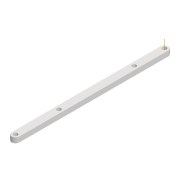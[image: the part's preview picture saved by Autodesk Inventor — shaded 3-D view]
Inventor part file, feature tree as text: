
AUTODESK INVENTOR PART (.ipt)
format: ipt  version: 2022 (Build 260153000, 153)  size: 94,208 bytes
history: native  units: mm
features: extrude x1, other x1, sketch x1
ambient origin geometry x8: Origin, YZ Plane, XZ Plane, XY Plane, X Axis, Y Axis, Z Axis, Center Point
bodies: Solid1 (feature_tree)
feature tree (3):
  extrude  "Extrusion1"  Depth=93.045mm
  other  "Work Axis1"
  sketch  "Sketch1"  dims[d0=3.2mm d1=3.2mm d2=6.0mm d3=116.749mm d4=3.2mm d5=33.922mm d6=4.0mm d7=0.0mm d8=3.2mm d9=93.045mm]
